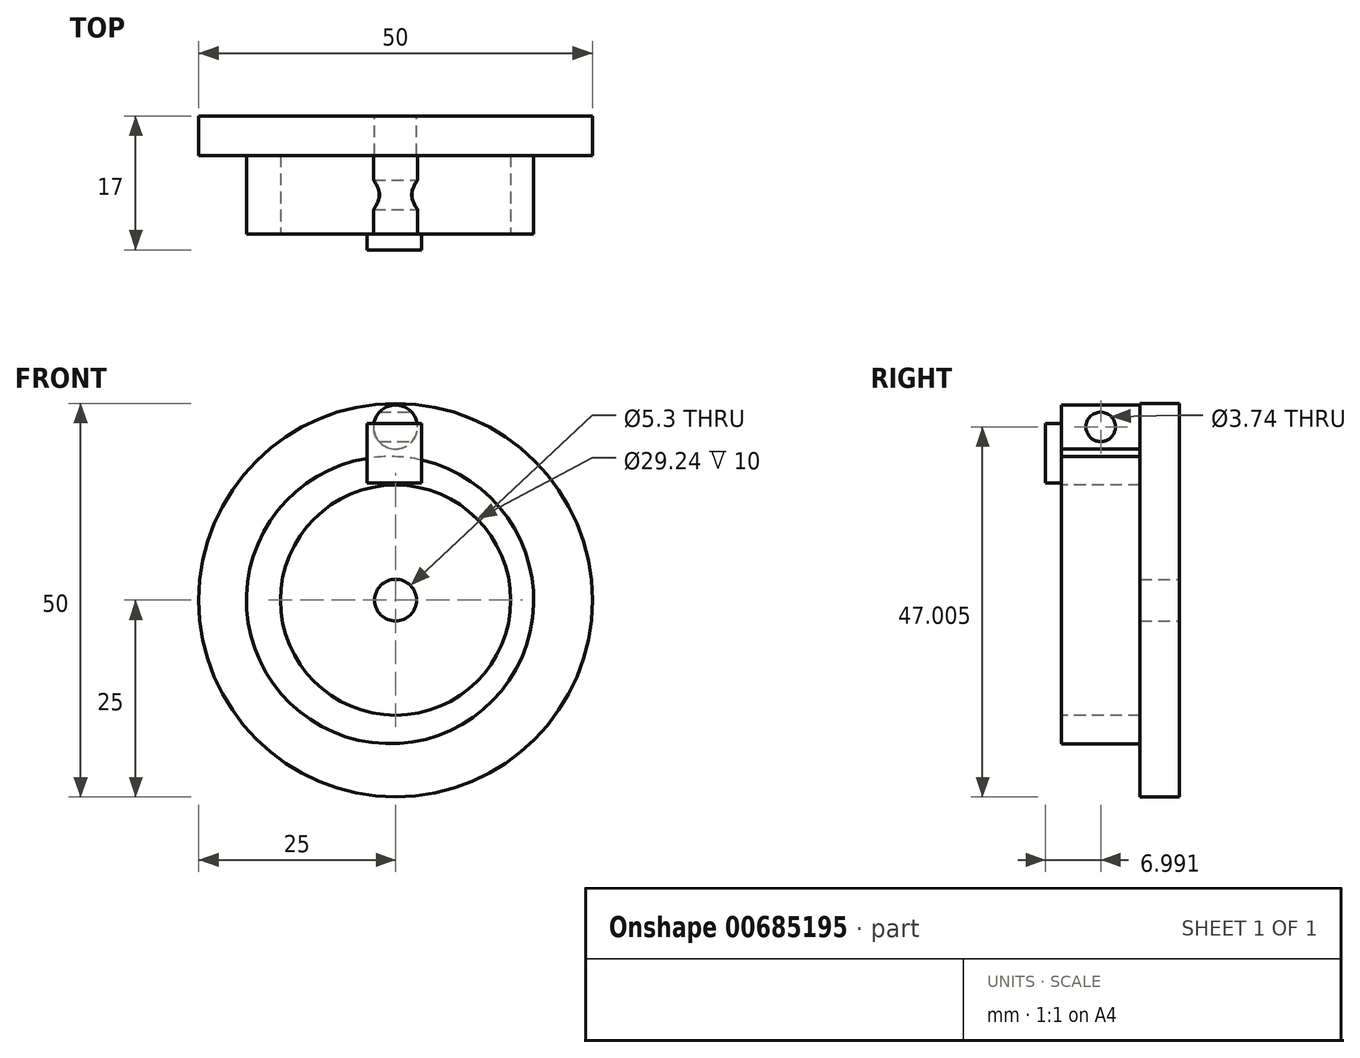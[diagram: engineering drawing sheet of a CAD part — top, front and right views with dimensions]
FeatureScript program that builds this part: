
annotation { "Feature Type Name" : "Feature", "Feature Type Description" : "" }
export const myFeature = defineFeature(function(context is Context, id is Id, definition is map)
    precondition{}
    {
        {
            var Q0;
            Q0=qCreatedBy(makeId("Front.planeOp"),FACE);
            var sketch = newSketch(context, id + "F0", { "sketchPlane" : qUnion([Q0])});
            skCircle(sketch, "E0", {"center": v(0, 0) * mm, "radius": 25 * mm});
            skSolve(sketch);
        }
        {
            var Q0;
            Q0=makeQuery(id+"F0.imprint","IMPRINT",FACE,{"disambiguationData":[TD([[makeQuery(id+"F0.imprint","IMPRINT",EDGE,{"derivedFrom":sQuery(id+"F0.wireOp",EDGE,"E0")}),1.0]])]});
            extrude(context, id + "F1", {"entities" : qUnion([Q0]), "depth" : 5 * mm, "offsetDistance" : 25.4 * mm});
        }
        {
            var Q0;
            Q0=makeQuery(id+"F1.opExtrude","CAP_FACE",FACE,{"disambiguationData":[OSD([sQuery(id+"F0.wireOp",EDGE,"E0")])],"isStart":true});
            var sketch = newSketch(context, id + "F2", { "sketchPlane" : qUnion([Q0])});
            skCircle(sketch, "E1", {"center": v(0, 0) * mm, "radius": 2.65 * mm});
            skSolve(sketch);
        }
        {
            var Q0;
            Q0 = qSketchRegion(id + "F2", true);
            extrude(context, id + "F3", {"entities" : qUnion([Q0]), "operationType" : NewBodyOperationType.REMOVE, "oppositeDirection" : true, "depth" : 5 * mm, "offsetDistance" : 25.4 * mm});
        }
        {
            var Q0;
            Q0=makeQuery(id+"F1.opExtrude","CAP_FACE",FACE,{"disambiguationData":[OSD([sQuery(id+"F0.wireOp",EDGE,"E0")])],"isStart":false});
            var sketch = newSketch(context, id + "F4", { "sketchPlane" : qUnion([Q0])});
            skCircle(sketch, "E2", {"center": v(-2.65, 0) * mm, "radius": 0.7 * mm});
            skCircle(sketch, "E3", {"center": v(0, 2.65) * mm, "radius": 0.68 * mm});
            skCircle(sketch, "E4", {"center": v(2.65, 0) * mm, "radius": 0.7 * mm});
            skCircle(sketch, "E5", {"center": v(0, -2.65) * mm, "radius": 0.7 * mm});
            skCircle(sketch, "E6", {"center": v(-2.27, 1.37) * mm, "radius": 0.7 * mm});
            skCircle(sketch, "E7", {"center": v(-1.3, 2.31) * mm, "radius": 0.7 * mm});
            skCircle(sketch, "E8", {"center": v(2.36, 1.2) * mm, "radius": 0.7 * mm});
            skCircle(sketch, "E9", {"center": v(1.45, 2.22) * mm, "radius": 0.7 * mm});
            skCircle(sketch, "E10", {"center": v(-2.33, -1.27) * mm, "radius": 0.7 * mm});
            skCircle(sketch, "E11", {"center": v(-1.27, -2.32) * mm, "radius": 0.71 * mm});
            skCircle(sketch, "E12", {"center": v(2.3, -1.3) * mm, "radius": 0.7 * mm});
            skCircle(sketch, "E13", {"center": v(1.37, -2.27) * mm, "radius": 0.7 * mm});
            skSolve(sketch);
        }
        {
            var Q0;
            Q0=makeQuery(id+"F1.opExtrude","CAP_FACE",FACE,{"disambiguationData":[OSD([sQuery(id+"F0.wireOp",EDGE,"E0")])],"isStart":false});
            var sketch = newSketch(context, id + "F5", { "sketchPlane" : qUnion([Q0])});
            skCircle(sketch, "E14", {"center": v(-0.7, 0) * mm, "radius": 18.24 * mm});
            skSolve(sketch);
        }
        {
            var Q0;
            Q0=makeQuery(id+"F5.imprint","IMPRINT",FACE,{"disambiguationData":[TD([[makeQuery(id+"F5.imprint","IMPRINT",EDGE,{"derivedFrom":sQuery(id+"F5.wireOp",EDGE,"E14")}),1.0]])]});
            var Q1;
            Q1=sQuery(id+"F5.wireOp",EDGE,"E14");
            extrude(context, id + "F6", {"entities" : qUnion([Q0]), "operationType" : NewBodyOperationType.ADD, "surfaceEntities" : qUnion([Q1]), "depth" : 10 * mm, "offsetDistance" : 25.4 * mm});
        }
        {
            var Q0;
            Q0=makeQuery(id+"F6.opExtrude","CAP_FACE",FACE,{"disambiguationData":[OSD([sQuery(id+"F2.wireOp",EDGE,"E1"),sQuery(id+"F4.wireOp",EDGE,"E2"),sQuery(id+"F4.wireOp",EDGE,"E3"),sQuery(id+"F4.wireOp",EDGE,"E4"),sQuery(id+"F4.wireOp",EDGE,"E5"),sQuery(id+"F4.wireOp",EDGE,"E6"),sQuery(id+"F4.wireOp",EDGE,"E7"),sQuery(id+"F4.wireOp",EDGE,"E8"),sQuery(id+"F4.wireOp",EDGE,"E9"),sQuery(id+"F4.wireOp",EDGE,"E10"),sQuery(id+"F4.wireOp",EDGE,"E11"),sQuery(id+"F4.wireOp",EDGE,"E12"),sQuery(id+"F4.wireOp",EDGE,"E13"),sQuery(id+"F5.wireOp",EDGE,"E14")])],"isStart":false});
            var sketch = newSketch(context, id + "F7", { "sketchPlane" : qUnion([Q0])});
            skCircle(sketch, "E15", {"center": v(0, 0) * mm, "radius": 14.62 * mm});
            skSolve(sketch);
        }
        {
            var Q0;
            Q0=makeQuery(id+"F7.imprint","IMPRINT",FACE,{"disambiguationData":[TD([[makeQuery(id+"F7.imprint","IMPRINT",EDGE,{"derivedFrom":sQuery(id+"F7.wireOp",EDGE,"E15")}),1.0]])]});
            extrude(context, id + "F8", {"entities" : qUnion([Q0]), "operationType" : NewBodyOperationType.REMOVE, "oppositeDirection" : true, "depth" : 10 * mm, "offsetDistance" : 25.4 * mm});
        }
        {
            var Q0;
            Q0=makeQuery(id+"F1.opExtrude","CAP_FACE",FACE,{"disambiguationData":[OSD([sQuery(id+"F0.wireOp",EDGE,"E0")])],"isStart":false});
            var sketch = newSketch(context, id + "F9", { "sketchPlane" : qUnion([Q0])});
            skCircle(sketch, "E16", {"center": v(0, 22) * mm, "radius": 2.79 * mm});
            skSolve(sketch);
        }
        {
            var Q0;
            Q0=makeQuery(id+"F9.imprint","IMPRINT",FACE,{"disambiguationData":[TD([[makeQuery(id+"F9.imprint","IMPRINT",EDGE,{"derivedFrom":sQuery(id+"F9.wireOp",EDGE,"E16")}),1.0]])]});
            extrude(context, id + "F10", {"entities" : qUnion([Q0]), "operationType" : NewBodyOperationType.ADD, "depth" : 10 * mm, "offsetDistance" : 25.4 * mm});
        }
        {
            var Q0;
            Q0=makeQuery(id+"F10.opExtrude","CAP_FACE",FACE,{"disambiguationData":[OSD([sQuery(id+"F9.wireOp",EDGE,"E16")])],"isStart":false});
            var sketch = newSketch(context, id + "F11", { "sketchPlane" : qUnion([Q0])});
            skLineSegment(sketch, "E17.bottom", {"start": v(-3.6, 22.45) * mm, "end": v(3.3, 22.45) * mm});
            skLineSegment(sketch, "E17.top", {"start": v(-3.6, 14.88) * mm, "end": v(3.3, 14.88) * mm});
            skLineSegment(sketch, "E17.left", {"start": v(-3.6, 22.45) * mm, "end": v(-3.6, 14.88) * mm});
            skLineSegment(sketch, "E17.right", {"start": v(3.3, 22.45) * mm, "end": v(3.3, 14.88) * mm});
            skSolve(sketch);
        }
        {
            var Q0;
            Q0=makeQuery(id+"F11.imprint","IMPRINT",FACE,{"disambiguationData":[TD([[makeQuery(id+"F11.imprint","IMPRINT",EDGE,{"derivedFrom":sQuery(id+"F11.wireOp",EDGE,"E17.top")}),1.0]])]});
            var Q1;
            {var subQ0=sQuery(id+"F11.wireOp",EDGE,"E17.bottom");var subQ1=makeQuery(id+"F10.opExtrude","CAP_EDGE",EDGE,{"disambiguationData":[OSD([sQuery(id+"F9.wireOp",EDGE,"E16")])],"isStart":false});var subQ2=makeQuery(id+"F11.imprint","INTERSECT",VERTEX,{"disambiguationData":[OD(0.0)],"derivedFrom":[subQ1,subQ0]});Q1=makeQuery(id+"F11.imprint","IMPRINT",FACE,{"disambiguationData":[TD([[makeQuery(id+"F11.imprint","IMPRINT",EDGE,{"disambiguationData":[TD([[subQ2,-1.0]])],"derivedFrom":subQ0}),-1.0]])]});}
            extrude(context, id + "F12", {"entities" : qUnion([Q0, Q1]), "operationType" : NewBodyOperationType.ADD, "depth" : 2 * mm, "offsetDistance" : 25.4 * mm});
        }
        {
            var Q0;
            Q0=makeQuery(id+"F12.opExtrude","SWEPT_FACE",FACE,{"disambiguationData":[OSD([sQuery(id+"F11.wireOp",EDGE,"E17.right")])]});
            var sketch = newSketch(context, id + "F13", { "sketchPlane" : qUnion([Q0])});
            skCircle(sketch, "E18", {"center": v(-10, 22) * mm, "radius": 1.87 * mm});
            skSolve(sketch);
        }
        {
            var Q0;
            Q0 = qSketchRegion(id + "F13", true);
            extrude(context, id + "F14", {"entities" : qUnion([Q0]), "operationType" : NewBodyOperationType.REMOVE, "oppositeDirection" : true, "depth" : 25.4 * mm, "offsetDistance" : 25.4 * mm});
        }
    });
